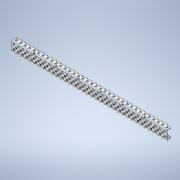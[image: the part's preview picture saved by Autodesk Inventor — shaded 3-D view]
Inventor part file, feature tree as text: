
AUTODESK INVENTOR PART (.ipt)
format: ipt  version: 2020 (Build 240168000, 168)  size: 1,500,672 bytes
history: native  units: in
note: dims shown in document units (in); Inventor stores cm internally (conversion verified against a paired STEP export)
features: other x178, plane x6, pattern_linear x4, sheet_metal_op x1
ambient origin geometry x8: Origin, YZ Plane, XZ Plane, XY Plane, X Axis, Y Axis, Z Axis, Center Point
bodies: Solid1 (feature_tree)
feature tree (189):
  other  "Work Axis1"
  pattern_linear  "Rectangular Pattern1"  Count1=35 Spacing1=0.5in
  other  "Work Axis72"
  pattern_linear  "Rectangular Pattern2"  Count1=2 Spacing1=0.5in
  pattern_linear  "Rectangular Pattern3"  Count1=35 Spacing1=0.5in
  other  "Work Axis141"
  pattern_linear  "Rectangular Pattern4"  Count1=35 Spacing1=0.5in
  plane  "Work Plane1"
  plane  "Work Plane2"
  other  "Work Point1"
  other  "Work Axis2"
  other  "Work Axis3"
  other  "Work Axis4"
  other  "Work Axis5"
  other  "Work Axis6"
  other  "Work Axis7"
  other  "Work Axis8"
  other  "Work Axis9"
  other  "Work Axis10"
  other  "Work Axis11"
  other  "Work Axis12"
  other  "Work Axis13"
  other  "Work Axis14"
  other  "Work Axis15"
  other  "Work Axis16"
  other  "Work Axis17"
  other  "Work Axis18"
  other  "Work Axis19"
  other  "Work Axis20"
  other  "Work Axis21"
  other  "Work Axis22"
  other  "Work Axis23"
  other  "Work Axis24"
  other  "Work Axis25"
  other  "Work Axis26"
  other  "Work Axis27"
  other  "Work Axis28"
  other  "Work Axis29"
  other  "Work Axis30"
  other  "Work Axis31"
  other  "Work Axis32"
  other  "Work Axis33"
  other  "Work Axis34"
  other  "Work Axis35"
  other  "Work Axis36"
  other  "Work Axis37"
  other  "Work Axis38"
  other  "Work Axis39"
  other  "Work Axis40"
  other  "Work Axis41"
  other  "Work Axis42"
  other  "Work Axis43"
  other  "Work Axis44"
  other  "Work Axis45"
  other  "Work Axis46"
  other  "Work Axis47"
  other  "Work Axis48"
  other  "Work Axis49"
  other  "Work Axis50"
  other  "Work Axis51"
  other  "Work Axis52"
  other  "Work Axis53"
  other  "Work Axis54"
  other  "Work Axis55"
  other  "Work Axis56"
  other  "Work Axis57"
  other  "Work Axis58"
  other  "Work Axis59"
  other  "Work Axis60"
  other  "Work Axis61"
  other  "Work Axis62"
  other  "Work Axis63"
  other  "Work Axis64"
  other  "Work Axis65"
  other  "Work Axis66"
  other  "Work Axis67"
  other  "Work Axis68"
  other  "Work Axis69"
  other  "Work Axis70"
  plane  "Work Plane3"
  plane  "Work Plane4"
  other  "Work Point2"
  other  "Work Axis71"
  other  "Work Point3"
  other  "Work Axis73"
  other  "Work Axis74"
  other  "Work Axis75"
  other  "Work Axis76"
  other  "Work Axis77"
  other  "Work Axis78"
  other  "Work Axis79"
  other  "Work Axis80"
  other  "Work Axis81"
  other  "Work Axis82"
  other  "Work Axis83"
  other  "Work Axis84"
  other  "Work Axis85"
  other  "Work Axis86"
  other  "Work Axis87"
  other  "Work Axis88"
  other  "Work Axis89"
  other  "Work Axis90"
  other  "Work Axis91"
  other  "Work Axis92"
  other  "Work Axis93"
  other  "Work Axis94"
  other  "Work Axis95"
  other  "Work Axis96"
  other  "Work Axis97"
  other  "Work Axis98"
  other  "Work Axis99"
  other  "Work Axis100"
  other  "Work Axis101"
  other  "Work Axis102"
  other  "Work Axis103"
  other  "Work Axis104"
  other  "Work Axis105"
  other  "Work Axis106"
  other  "Work Axis107"
  other  "Work Axis108"
  other  "Work Axis109"
  other  "Work Axis110"
  other  "Work Axis111"
  other  "Work Axis112"
  other  "Work Axis113"
  other  "Work Axis114"
  other  "Work Axis115"
  other  "Work Axis116"
  other  "Work Axis117"
  other  "Work Axis118"
  other  "Work Axis119"
  other  "Work Axis120"
  other  "Work Axis121"
  other  "Work Axis122"
  other  "Work Axis123"
  other  "Work Axis124"
  other  "Work Axis125"
  other  "Work Axis126"
  other  "Work Axis127"
  other  "Work Axis128"
  other  "Work Axis129"
  other  "Work Axis130"
  other  "Work Axis131"
  other  "Work Axis132"
  other  "Work Axis133"
  other  "Work Axis134"
  other  "Work Axis135"
  other  "Work Axis136"
  other  "Work Axis137"
  other  "Work Axis138"
  other  "Work Axis139"
  other  "Work Axis140"
  plane  "Work Plane5"
  plane  "Work Plane6"
  other  "Work Point4"
  other  "Work Axis142"
  other  "Work Axis143"
  other  "Work Axis144"
  other  "Work Axis145"
  other  "Work Axis146"
  other  "Work Axis147"
  other  "Work Axis148"
  other  "Work Axis149"
  other  "Work Axis150"
  other  "Work Axis151"
  other  "Work Axis152"
  other  "Work Axis153"
  other  "Work Axis154"
  other  "Work Axis155"
  other  "Work Axis156"
  other  "Work Axis157"
  other  "Work Axis158"
  other  "Work Axis159"
  other  "Work Axis160"
  other  "Work Axis161"
  other  "Work Axis162"
  other  "Work Axis163"
  other  "Work Axis164"
  other  "Work Axis165"
  other  "Work Axis166"
  other  "Work Axis167"
  other  "Work Axis168"
  other  "Work Axis169"
  other  "Work Axis170"
  other  "Work Axis171"
  other  "Work Axis172"
  other  "Work Axis173"
  other  "Work Axis174"
  sheet_metal_op  "Fold1"
